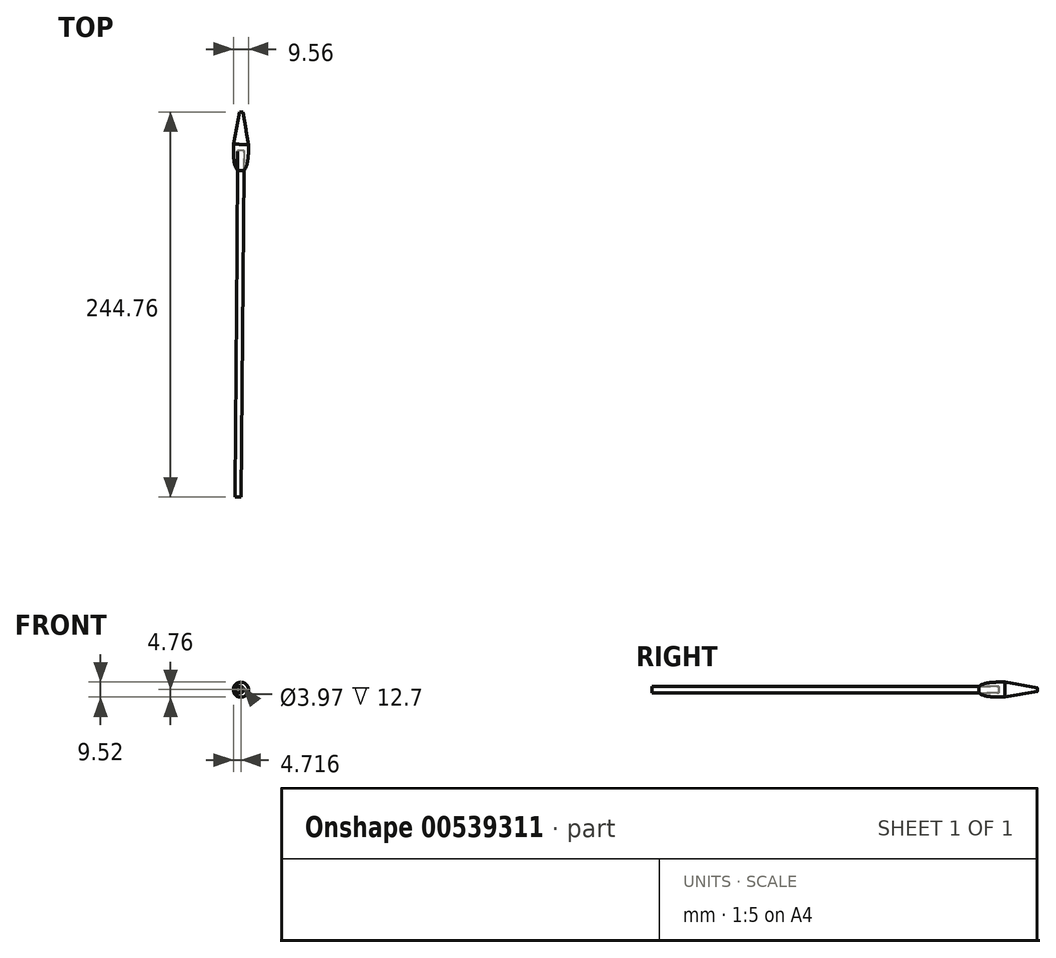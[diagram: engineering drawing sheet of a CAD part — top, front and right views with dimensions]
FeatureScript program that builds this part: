
annotation { "Feature Type Name" : "Feature", "Feature Type Description" : "" }
export const myFeature = defineFeature(function(context is Context, id is Id, definition is map)
    precondition{}
    {
        {
            var Q0;
            Q0=qCreatedBy(makeId("Top.planeOp"),FACE);
            var sketch = newSketch(context, id + "F0", { "sketchPlane" : qUnion([Q0])});
            skLineSegment(sketch, "E0", {"start": v(16.72, 39.09) * mm, "end": v(14.58, -13.25) * mm, "construction": true});
            skLineSegment(sketch, "E1", {"start": v(25.02, 11.07) * mm, "end": v(23.35, -196.37) * mm});
            skLineSegment(sketch, "E2", {"start": v(25.02, 11.07) * mm, "end": v(25.33, 48.37) * mm});
            skLineSegment(sketch, "E3", {"start": v(21.36, -196.35) * mm, "end": v(23.35, -196.37) * mm});
            skLineSegment(sketch, "E4", {"start": v(21.36, -196.35) * mm, "end": v(23.04, 11.08) * mm});
            skLineSegment(sketch, "E5", {"start": v(23.04, 11.08) * mm, "end": v(25.02, 11.07) * mm, "construction": true});
            skLineSegment(sketch, "E6", {"start": v(25.33, 48.37) * mm, "end": v(24.23, 48.38) * mm});
            skLineSegment(sketch, "E7", {"start": v(24.23, 48.38) * mm, "end": v(20.4, 27.77) * mm});
            skLineSegment(sketch, "E8", {"start": v(20.36, 23.01) * mm, "end": v(20.4, 27.77) * mm});
            skLineSegment(sketch, "E9", {"start": v(21.06, 15.22) * mm, "end": v(20.36, 23.01) * mm, "construction": true});
            skLineSegment(sketch, "E10", {"start": v(23.04, 11.08) * mm, "end": v(21.72, 12.6) * mm, "construction": true});
            skLineSegment(sketch, "E11", {"start": v(21.72, 12.6) * mm, "end": v(21.06, 15.22) * mm, "construction": true});
            skLineSegment(sketch, "E12", {"start": v(23.04, 11.08) * mm, "end": v(23.14, 23.78) * mm});
            skLineSegment(sketch, "E13", {"start": v(23.14, 23.78) * mm, "end": v(25.13, 23.77) * mm});
            skFitSpline(sketch, "E14", {"points": [v(20.36, 23.01) * mm, v(21.3, 14.6) * mm, v(23.04, 11.08) * mm], "startDerivative": vector(-0.12, -14.89) * mm, "endDerivative": vector(6.16, -8.75) * mm});
            skSolve(sketch);
        }
        {
            var Q0;
            {var subQ1=sQuery(id+"F0.wireOp",EDGE,"E1");Q0=makeQuery(id+"F0.imprint","IMPRINT",FACE,{"disambiguationData":[TD([[makeQuery(id+"F0.imprint","IMPRINT",EDGE,{"derivedFrom":subQ1}),-1.0]])]});}
            var Q1;
            Q1=sQuery(id+"F0.wireOp",EDGE,"E1");
            revolve(context, id + "F1", {"surfaceOperationType" : NewSurfaceOperationType.NEW, "entities" : qUnion([Q0]), "axis" : qUnion([Q1]), "revolveType" : RevolveType.FULL});
        }
        {
            var Q0;
            {var subQ0=sQuery(id+"F0.wireOp",EDGE,"E6");Q0=makeQuery(id+"F0.imprint","IMPRINT",FACE,{"disambiguationData":[TD([[makeQuery(id+"F0.imprint","IMPRINT",EDGE,{"derivedFrom":subQ0}),1.0]])]});}
            var Q1;
            Q1=sQuery(id+"F0.wireOp",EDGE,"E2");
            revolve(context, id + "F2", {"surfaceOperationType" : NewSurfaceOperationType.NEW, "entities" : qUnion([Q0]), "axis" : qUnion([Q1]), "revolveType" : RevolveType.FULL});
        }
    });
